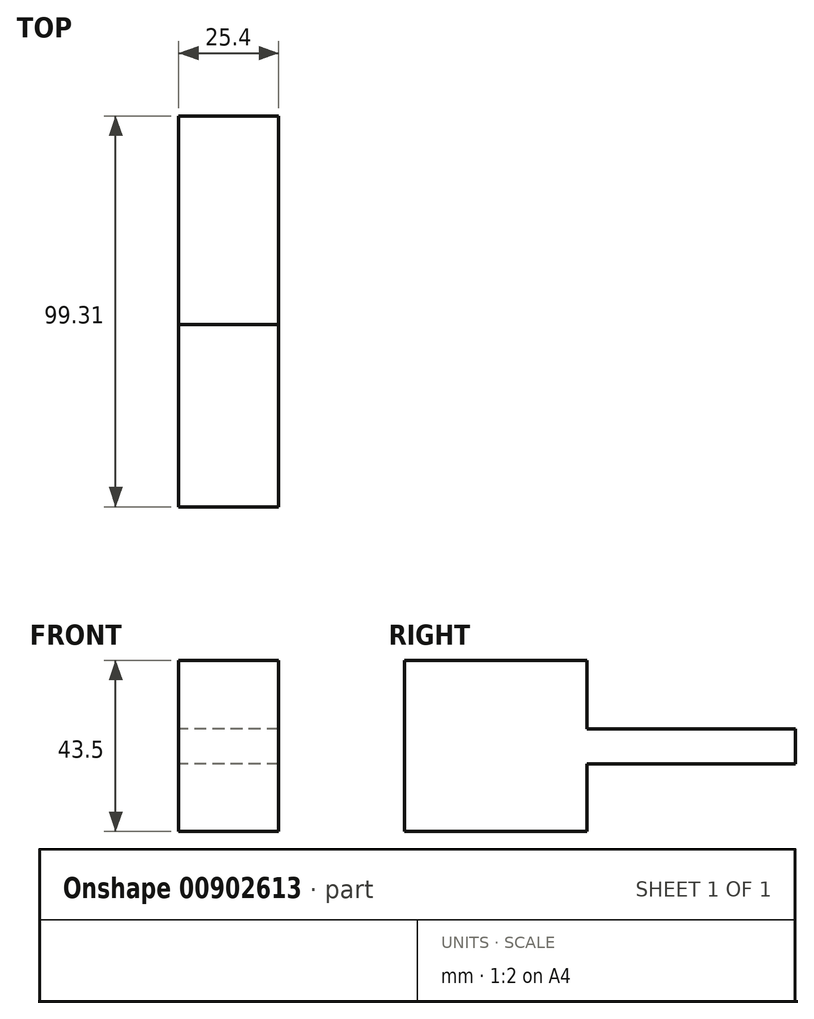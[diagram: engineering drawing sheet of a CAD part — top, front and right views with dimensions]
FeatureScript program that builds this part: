
annotation { "Feature Type Name" : "Feature", "Feature Type Description" : "" }
export const myFeature = defineFeature(function(context is Context, id is Id, definition is map)
    precondition{}
    {
        {
            var Q0;
            Q0=qCreatedBy(makeId("Right.planeOp"),FACE);
            var sketch = newSketch(context, id + "F0", { "sketchPlane" : qUnion([Q0])});
            skLineSegment(sketch, "E0.bottom", {"start": v(-23.14, -21.75) * mm, "end": v(23.14, -21.75) * mm});
            skLineSegment(sketch, "E0.top", {"start": v(-23.14, 21.75) * mm, "end": v(23.14, 21.75) * mm});
            skLineSegment(sketch, "E0.left", {"start": v(-23.14, -21.75) * mm, "end": v(-23.14, 21.75) * mm});
            skLineSegment(sketch, "E0.right", {"start": v(23.14, -21.75) * mm, "end": v(23.14, 21.75) * mm});
            skPoint(sketch, "E0.middle", {"position": v(0, 0) * mm});
            skLineSegment(sketch, "E1.bottom", {"start": v(23.14, 4.3) * mm, "end": v(76.17, 4.3) * mm});
            skLineSegment(sketch, "E1.top", {"start": v(23.14, -4.54) * mm, "end": v(76.17, -4.54) * mm});
            skLineSegment(sketch, "E1.left", {"start": v(23.14, 4.3) * mm, "end": v(23.14, -4.54) * mm});
            skLineSegment(sketch, "E1.right", {"start": v(76.17, 4.3) * mm, "end": v(76.17, -4.54) * mm});
            skSolve(sketch);
        }
        {
            var Q0;
            {var subQ1=sQuery(id+"F0.wireOp",EDGE,"E0.bottom");Q0=makeQuery(id+"F0.imprint","IMPRINT",FACE,{"disambiguationData":[TD([[makeQuery(id+"F0.imprint","IMPRINT",EDGE,{"derivedFrom":subQ1}),1.0]])]});}
            var Q1;
            Q1=makeQuery(id+"F0.imprint","IMPRINT",FACE,{"disambiguationData":[TD([[makeQuery(id+"F0.imprint","IMPRINT",EDGE,{"derivedFrom":sQuery(id+"F0.wireOp",EDGE,"E1.bottom")}),-1.0]])]});
            extrude(context, id + "F1", {"entities" : qUnion([Q0, Q1]), "depth" : 25.4 * mm, "offsetDistance" : 25.4 * mm});
        }
    });
